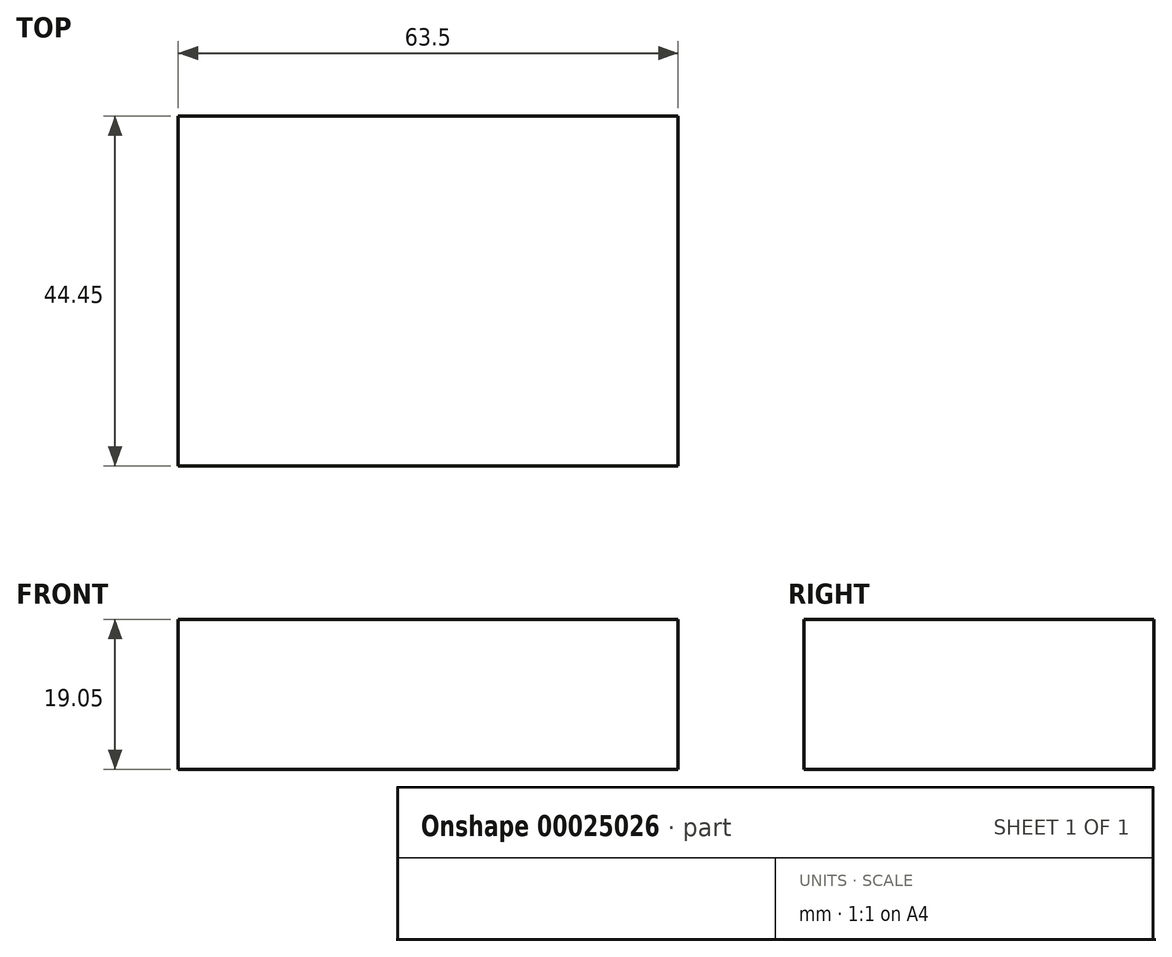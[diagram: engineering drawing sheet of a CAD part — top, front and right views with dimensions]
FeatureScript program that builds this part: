
annotation { "Feature Type Name" : "Feature", "Feature Type Description" : "" }
export const myFeature = defineFeature(function(context is Context, id is Id, definition is map)
    precondition{}
    {
        {
            var Q0;
            Q0=qCreatedBy(makeId("Front.planeOp"),FACE);
            var sketch = newSketch(context, id + "F0", { "sketchPlane" : qUnion([Q0])});
            skLineSegment(sketch, "E0.bottom", {"start": v(-58.38, 19.7) * mm, "end": v(5.12, 19.7) * mm});
            skLineSegment(sketch, "E0.top", {"start": v(-58.38, 0.66) * mm, "end": v(5.12, 0.66) * mm});
            skLineSegment(sketch, "E0.left", {"start": v(-58.38, 19.7) * mm, "end": v(-58.38, 0.66) * mm});
            skLineSegment(sketch, "E0.right", {"start": v(5.12, 19.7) * mm, "end": v(5.12, 0.66) * mm});
            skSolve(sketch);
        }
        {
            var Q0;
            Q0 = qSketchRegion(id + "F0", true);
            extrude(context, id + "F1", {"entities" : qUnion([Q0]), "depth" : 44.45 * mm});
        }
    });
